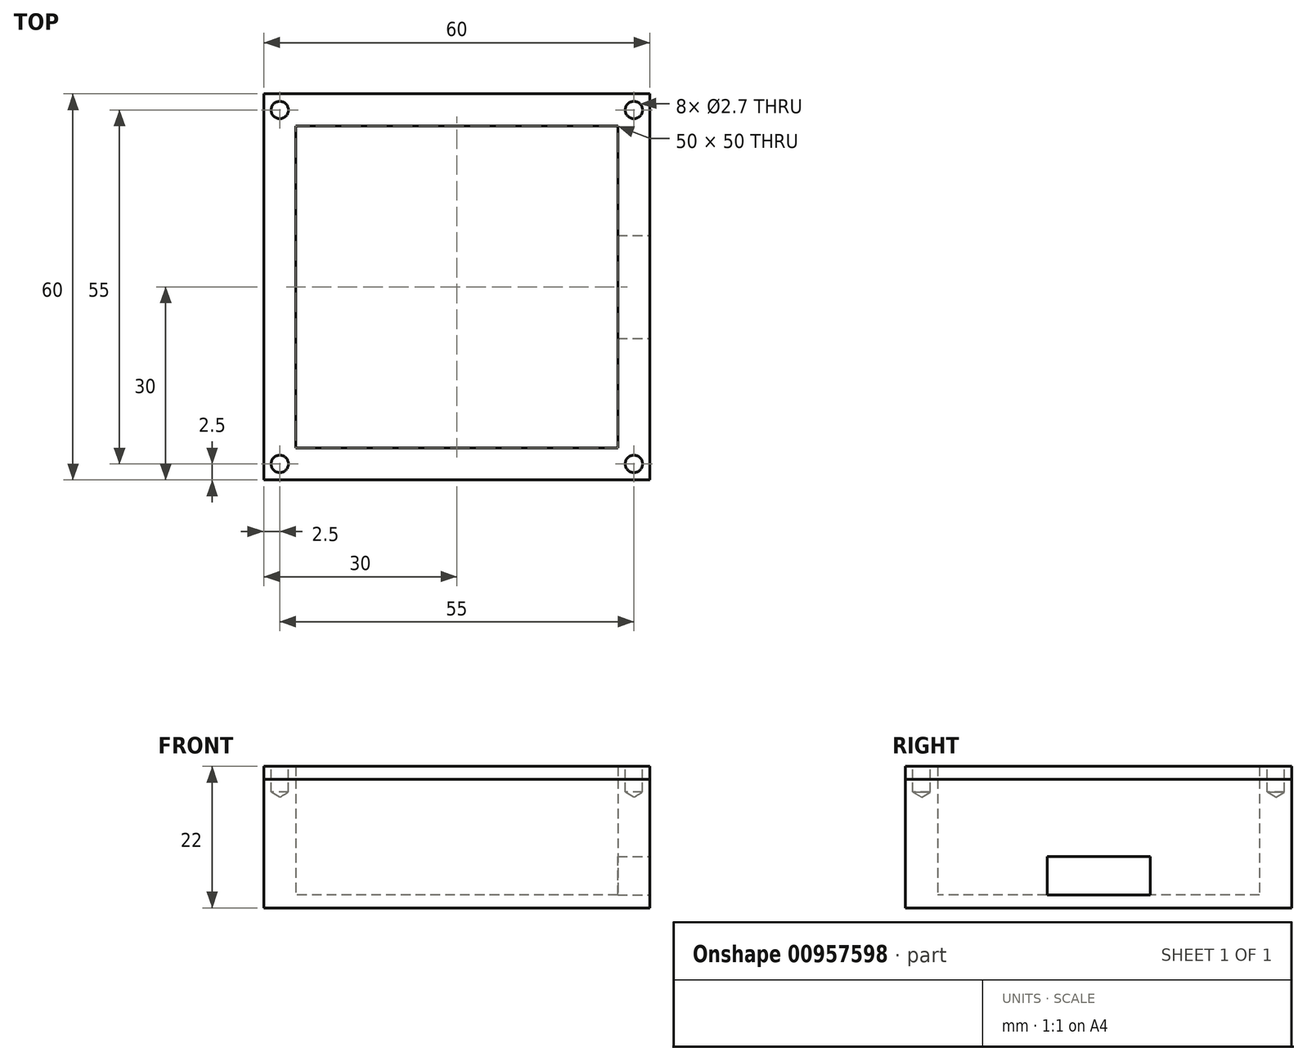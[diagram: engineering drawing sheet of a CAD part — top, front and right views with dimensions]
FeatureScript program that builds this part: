
annotation { "Feature Type Name" : "Feature", "Feature Type Description" : "" }
export const myFeature = defineFeature(function(context is Context, id is Id, definition is map)
    precondition{}
    {
        {
            var Q0;
            Q0=qCreatedBy(makeId("Top.planeOp"),FACE);
            var sketch = newSketch(context, id + "F0", { "sketchPlane" : qUnion([Q0])});
            skLineSegment(sketch, "E0.bottom", {"start": v(25, 25) * mm, "end": v(-25, 25) * mm});
            skLineSegment(sketch, "E0.top", {"start": v(25, -25) * mm, "end": v(-25, -25) * mm});
            skLineSegment(sketch, "E0.left", {"start": v(25, 25) * mm, "end": v(25, -25) * mm});
            skLineSegment(sketch, "E0.right", {"start": v(-25, 25) * mm, "end": v(-25, -25) * mm});
            skPoint(sketch, "E0.middle", {"position": v(0, 0) * mm});
            skLineSegment(sketch, "E1.bottom", {"start": v(30, -30) * mm, "end": v(-30, -30) * mm});
            skLineSegment(sketch, "E1.top", {"start": v(30, 30) * mm, "end": v(-30, 30) * mm});
            skLineSegment(sketch, "E1.left", {"start": v(30, -30) * mm, "end": v(30, 30) * mm});
            skLineSegment(sketch, "E1.right", {"start": v(-30, -30) * mm, "end": v(-30, 30) * mm});
            skSolve(sketch);
        }
        {
            var Q0;
            Q0=makeQuery(id+"F0.imprint","IMPRINT",FACE,{"disambiguationData":[TD([[makeQuery(id+"F0.imprint","IMPRINT",EDGE,{"derivedFrom":sQuery(id+"F0.wireOp",EDGE,"E0.bottom")}),-1.0]])]});
            extrude(context, id + "F1", {"entities" : qUnion([Q0]), "depth" : 18 * mm, "offsetDistance" : 25 * mm});
        }
        {
            var Q0;
            Q0=makeQuery(id+"F0.imprint","IMPRINT",FACE,{"disambiguationData":[TD([[makeQuery(id+"F0.imprint","IMPRINT",EDGE,{"derivedFrom":sQuery(id+"F0.wireOp",EDGE,"E0.bottom")}),-1.0]])]});
            var Q1;
            Q1=makeQuery(id+"F0.imprint","IMPRINT",FACE,{"disambiguationData":[TD([[makeQuery(id+"F0.imprint","IMPRINT",EDGE,{"derivedFrom":sQuery(id+"F0.wireOp",EDGE,"E0.bottom")}),1.0]])]});
            extrude(context, id + "F2", {"entities" : qUnion([Q0, Q1]), "operationType" : NewBodyOperationType.ADD, "oppositeDirection" : true, "depth" : 2 * mm, "offsetDistance" : 25 * mm});
        }
        {
            var Q0;
            {var subQ0=sQuery(id+"F0.wireOp",EDGE,"E1.left");Q0=makeQuery(id+"F2.boolean.opBoolean","MERGE",FACE,{"derivedFrom":[makeQuery(id+"F1.opExtrude","SWEPT_FACE",FACE,{"disambiguationData":[OSD([subQ0])]}),makeQuery(id+"F2.opExtrude","SWEPT_FACE",FACE,{"disambiguationData":[OSD([subQ0])]})]});}
            var sketch = newSketch(context, id + "F3", { "sketchPlane" : qUnion([Q0])});
            skLineSegment(sketch, "E2.bottom", {"start": v(-7.98, 6) * mm, "end": v(8.02, 6) * mm});
            skLineSegment(sketch, "E2.top", {"start": v(-7.98, 0) * mm, "end": v(8.02, 0) * mm});
            skLineSegment(sketch, "E2.left", {"start": v(-7.98, 6) * mm, "end": v(-7.98, 0) * mm});
            skLineSegment(sketch, "E2.right", {"start": v(8.02, 6) * mm, "end": v(8.02, 0) * mm});
            skLineSegment(sketch, "E3", {"start": v(-7.98, -2) * mm, "end": v(-7.98, 8) * mm, "construction": true});
            skLineSegment(sketch, "E4", {"start": v(8.02, -2) * mm, "end": v(8.02, 8) * mm, "construction": true});
            skLineSegment(sketch, "E5", {"start": v(-30, 6) * mm, "end": v(-7.98, 6) * mm, "construction": true});
            skLineSegment(sketch, "E6", {"start": v(8.02, 6) * mm, "end": v(30, 6) * mm, "construction": true});
            skSolve(sketch);
        }
        {
            var Q0;
            Q0=makeQuery(id+"F3.imprint","IMPRINT",FACE,{"disambiguationData":[TD([[makeQuery(id+"F3.imprint","IMPRINT",EDGE,{"derivedFrom":sQuery(id+"F3.wireOp",EDGE,"E2.bottom")}),-1.0]])]});
            extrude(context, id + "F4", {"entities" : qUnion([Q0]), "operationType" : NewBodyOperationType.REMOVE, "endBound" : BoundingType.UP_TO_NEXT, "oppositeDirection" : true, "depth" : 25 * mm, "offsetDistance" : 25 * mm});
        }
        {
            var Q0;
            Q0=makeQuery(id+"F1.opExtrude","CAP_FACE",FACE,{"disambiguationData":[OSD([sQuery(id+"F0.wireOp",EDGE,"E0.bottom"),sQuery(id+"F0.wireOp",EDGE,"E0.top"),sQuery(id+"F0.wireOp",EDGE,"E0.left"),sQuery(id+"F0.wireOp",EDGE,"E0.right"),sQuery(id+"F0.wireOp",EDGE,"E1.bottom"),sQuery(id+"F0.wireOp",EDGE,"E1.top"),sQuery(id+"F0.wireOp",EDGE,"E1.left"),sQuery(id+"F0.wireOp",EDGE,"E1.right")])],"isStart":false});
            var sketch = newSketch(context, id + "F5", { "sketchPlane" : qUnion([Q0])});
            skLineSegment(sketch, "E7.bottom", {"start": v(-30, -30) * mm, "end": v(30, -30) * mm});
            skLineSegment(sketch, "E7.top", {"start": v(-30, 30) * mm, "end": v(30, 30) * mm});
            skLineSegment(sketch, "E7.left", {"start": v(-30, -30) * mm, "end": v(-30, 30) * mm});
            skLineSegment(sketch, "E7.right", {"start": v(30, -30) * mm, "end": v(30, 30) * mm});
            skPoint(sketch, "E8.middle", {"position": v(0, 0) * mm});
            skCircle(sketch, "E9", {"center": v(0, 0) * mm, "radius": 21.5 * mm});
            skLineSegment(sketch, "E10.bottom", {"start": v(-25, 21.5) * mm, "end": v(25, 21.5) * mm});
            skLineSegment(sketch, "E10.top", {"start": v(-25, 17.5) * mm, "end": v(25, 17.5) * mm});
            skLineSegment(sketch, "E10.left", {"start": v(-25, 21.5) * mm, "end": v(-25, 17.5) * mm});
            skLineSegment(sketch, "E10.right", {"start": v(25, 21.5) * mm, "end": v(25, 17.5) * mm});
            skLineSegment(sketch, "E11.bottom", {"start": v(-25, -21.5) * mm, "end": v(25, -21.5) * mm});
            skLineSegment(sketch, "E11.top", {"start": v(-25, -17.5) * mm, "end": v(25, -17.5) * mm});
            skLineSegment(sketch, "E11.left", {"start": v(-25, -21.5) * mm, "end": v(-25, -17.5) * mm});
            skLineSegment(sketch, "E11.right", {"start": v(25, -21.5) * mm, "end": v(25, -17.5) * mm});
            skSolve(sketch);
        }
        {
            var Q0;
            Q0=makeQuery(id+"F5.imprint","IMPRINT",FACE,{"disambiguationData":[TD([[makeQuery(id+"F5.imprint","IMPRINT",EDGE,{"derivedFrom":sQuery(id+"F5.wireOp",EDGE,"E8.bottom")}),1.0]])]});
            var Q1;
            Q1=makeQuery(id+"F5.imprint","IMPRINT",FACE,{"disambiguationData":[TD([[makeQuery(id+"F5.imprint","IMPRINT",EDGE,{"derivedFrom":sQuery(id+"F5.wireOp",EDGE,"E7.bottom")}),-1.0]])]});
            extrude(context, id + "F6", {"entities" : qUnion([Q0, Q1]), "depth" : 2 * mm, "offsetDistance" : 25 * mm});
        }
        {
            var Q0;
            Q0=makeQuery(id+"F6.opExtrude","CAP_FACE",FACE,{"disambiguationData":[OSD([sQuery(id+"F5.wireOp",EDGE,"E7.bottom"),sQuery(id+"F5.wireOp",EDGE,"E7.top"),sQuery(id+"F5.wireOp",EDGE,"E7.left"),sQuery(id+"F5.wireOp",EDGE,"E7.right"),sQuery(id+"F5.wireOp",EDGE,"E8.bottom"),sQuery(id+"F5.wireOp",EDGE,"E8.top"),sQuery(id+"F5.wireOp",EDGE,"E8.left"),sQuery(id+"F5.wireOp",EDGE,"E8.right")])],"isStart":false});
            var sketch = newSketch(context, id + "F7", { "sketchPlane" : qUnion([Q0])});
            skPoint(sketch, "E12.middle", {"position": v(0, 0) * mm});
            skSolve(sketch);
        }
        {
            var Q0;
            {var subQ0=sQuery(id+"F7.wireOp",EDGE,"YlXVCEPd-yaDa-VcNV-erDy-wPVN3MQgXjY7.top");var subQ1=sQuery(id+"F7.wireOp",EDGE,"E12.top");var subQ2=sQuery(id+"F7.wireOp",EDGE,"YlXVCEPd-yaDa-VcNV-erDy-wPVN3MQgXjY7.bottom");var subQ3=sQuery(id+"F7.wireOp",EDGE,"E12.bottom");var subQ4=sQuery(id+"F5.wireOp",EDGE,"E8.right");var subQ5=sQuery(id+"F5.wireOp",EDGE,"E8.left");var subQ6=sQuery(id+"F5.wireOp",EDGE,"E8.top");var subQ7=sQuery(id+"F5.wireOp",EDGE,"E8.bottom");var subQ8=sQuery(id+"F5.wireOp",EDGE,"E7.right");var subQ9=sQuery(id+"F5.wireOp",EDGE,"E7.left");var subQ10=sQuery(id+"F5.wireOp",EDGE,"E7.top");var subQ11=sQuery(id+"F5.wireOp",EDGE,"E7.bottom");var subQ12=makeQuery(id+"F6.opExtrude","CAP_FACE",FACE,{"disambiguationData":[OSD([subQ11,subQ10,subQ9,subQ8,subQ7,subQ6,subQ5,subQ4])],"isStart":false});Q0=makeQuery(id+"FsvZpyolvliTNel_2.boolean.opBoolean","MERGE",FACE,{"derivedFrom":[makeQuery(id+"FdNc8r0Yi0niUzu_2.boolean.opBoolean","SPLIT",FACE,{"disambiguationData":[TD([makeQuery(id+"F6.opExtrude","SWEPT_FACE",FACE,{"disambiguationData":[OSD([subQ11])]})])],"derivedFrom":subQ12}),makeQuery(id+"FdNc8r0Yi0niUzu_2.boolean.opBoolean","SPLIT",FACE,{"disambiguationData":[TD([makeQuery(id+"F6.opExtrude","SWEPT_FACE",FACE,{"disambiguationData":[OSD([subQ7])]})])],"derivedFrom":subQ12})],"fromTools":[makeQuery(id+"FsvZpyolvliTNel_2.opExtrude","CAP_FACE",FACE,{"disambiguationData":[OSD([subQ3,subQ2,sQuery(id+"FuAVnFSXFe1YHzx.wireOp",EDGE,"113901e2-fc5f-4e8e-bcd3-d28b2fcaf334"),sQuery(id+"FuAVnFSXFe1YHzx.wireOp",EDGE,"bff0d37c-e628-420c-a2ad-2cd056d2ba32.MirrorCS")])],"isStart":false}),makeQuery(id+"FsvZpyolvliTNel_2.opExtrude","CAP_FACE",FACE,{"disambiguationData":[OSD([subQ1,subQ0,sQuery(id+"FuAVnFSXFe1YHzx.wireOp",EDGE,"342d736a-74e6-4a11-b634-af1b833943a9.MirrorCS"),sQuery(id+"FuAVnFSXFe1YHzx.wireOp",EDGE,"005a2a57-d4a7-4605-a5c6-7f1c0c94fffc.MirrorCS")])],"isStart":false})]});}
            var sketch = newSketch(context, id + "F8", { "sketchPlane" : qUnion([Q0])});
            skLineSegment(sketch, "E13", {"start": v(-30, 30) * mm, "end": v(-25, 25) * mm, "construction": true});
            skPoint(sketch, "E14", {"position": v(-27.5, 27.5) * mm});
            skLineSegment(sketch, "E15.MirrorCS", {"start": v(30, 30) * mm, "end": v(25, 25) * mm, "construction": true});
            skPoint(sketch, "E16.MirrorP", {"position": v(27.5, 27.5) * mm});
            skLineSegment(sketch, "E17.MirrorCS", {"start": v(30, -30) * mm, "end": v(25, -25) * mm, "construction": true});
            skPoint(sketch, "E18.MirrorP", {"position": v(27.5, -27.5) * mm});
            skLineSegment(sketch, "E19.MirrorCS", {"start": v(-30, -30) * mm, "end": v(-25, -25) * mm, "construction": true});
            skPoint(sketch, "E20.MirrorP", {"position": v(-27.5, -27.5) * mm});
            skSolve(sketch);
        }
        {
            var Q0;
            Q0=sQuery(id+"F8.wireOp",VERTEX,"E14");
            var Q1;
            Q1=sQuery(id+"F8.wireOp",VERTEX,"E16.MirrorP");
            var Q2;
            Q2=sQuery(id+"F8.wireOp",VERTEX,"E20.MirrorP");
            var Q3;
            Q3=sQuery(id+"F8.wireOp",VERTEX,"E18.MirrorP");
            var Q4;
            Q4=makeQuery(id+"F1.opExtrude","SWEPT_BODY",BODY,{"disambiguationData":[OSD([sQuery(id+"F0.wireOp",EDGE,"E0.bottom"),sQuery(id+"F0.wireOp",EDGE,"E0.top"),sQuery(id+"F0.wireOp",EDGE,"E0.left"),sQuery(id+"F0.wireOp",EDGE,"E0.right"),sQuery(id+"F0.wireOp",EDGE,"E1.bottom"),sQuery(id+"F0.wireOp",EDGE,"E1.top"),sQuery(id+"F0.wireOp",EDGE,"E1.left"),sQuery(id+"F0.wireOp",EDGE,"E1.right")])]});
            var Q5;
            Q5=makeQuery(id+"F6.opExtrude","SWEPT_BODY",BODY,{"disambiguationData":[OSD([sQuery(id+"F5.wireOp",EDGE,"E7.bottom"),sQuery(id+"F5.wireOp",EDGE,"E7.top"),sQuery(id+"F5.wireOp",EDGE,"E7.left"),sQuery(id+"F5.wireOp",EDGE,"E7.right"),sQuery(id+"F5.wireOp",EDGE,"E8.bottom"),sQuery(id+"F5.wireOp",EDGE,"E8.top"),sQuery(id+"F5.wireOp",EDGE,"E8.left"),sQuery(id+"F5.wireOp",EDGE,"E8.right")])]});
            hole(context, id + "F9", {"style" : HoleStyle.SIMPLE, "endStyle" : HoleEndStyle.BLIND, "standardTappedOrClearance" : lookupTablePath({ "standard" : "ISO", "engagement" : "50%", "pitch" : "0.5 mm", "size" : "M3", "type" : "Tapped" }), "standardBlindInLast" : lookupTablePath({ "standard" : "ISO", "fit" : "Normal", "engagement" : "50%", "pitch" : "0.5 mm", "size" : "M3", "type" : "Clearance & tapped" }), "holeDiameter" : 2.7 * mm, "majorDiameter" : 3 * mm, "showTappedDepth" : true, "holeDepth" : 4 * mm, "isTappedThrough" : true, "tappedDepth" : 2.5 * mm, "tapClearance" : 3, "locations" : qUnion([Q0, Q1, Q2, Q3]), "scope" : qUnion([Q4, Q5])});
        }
    });
